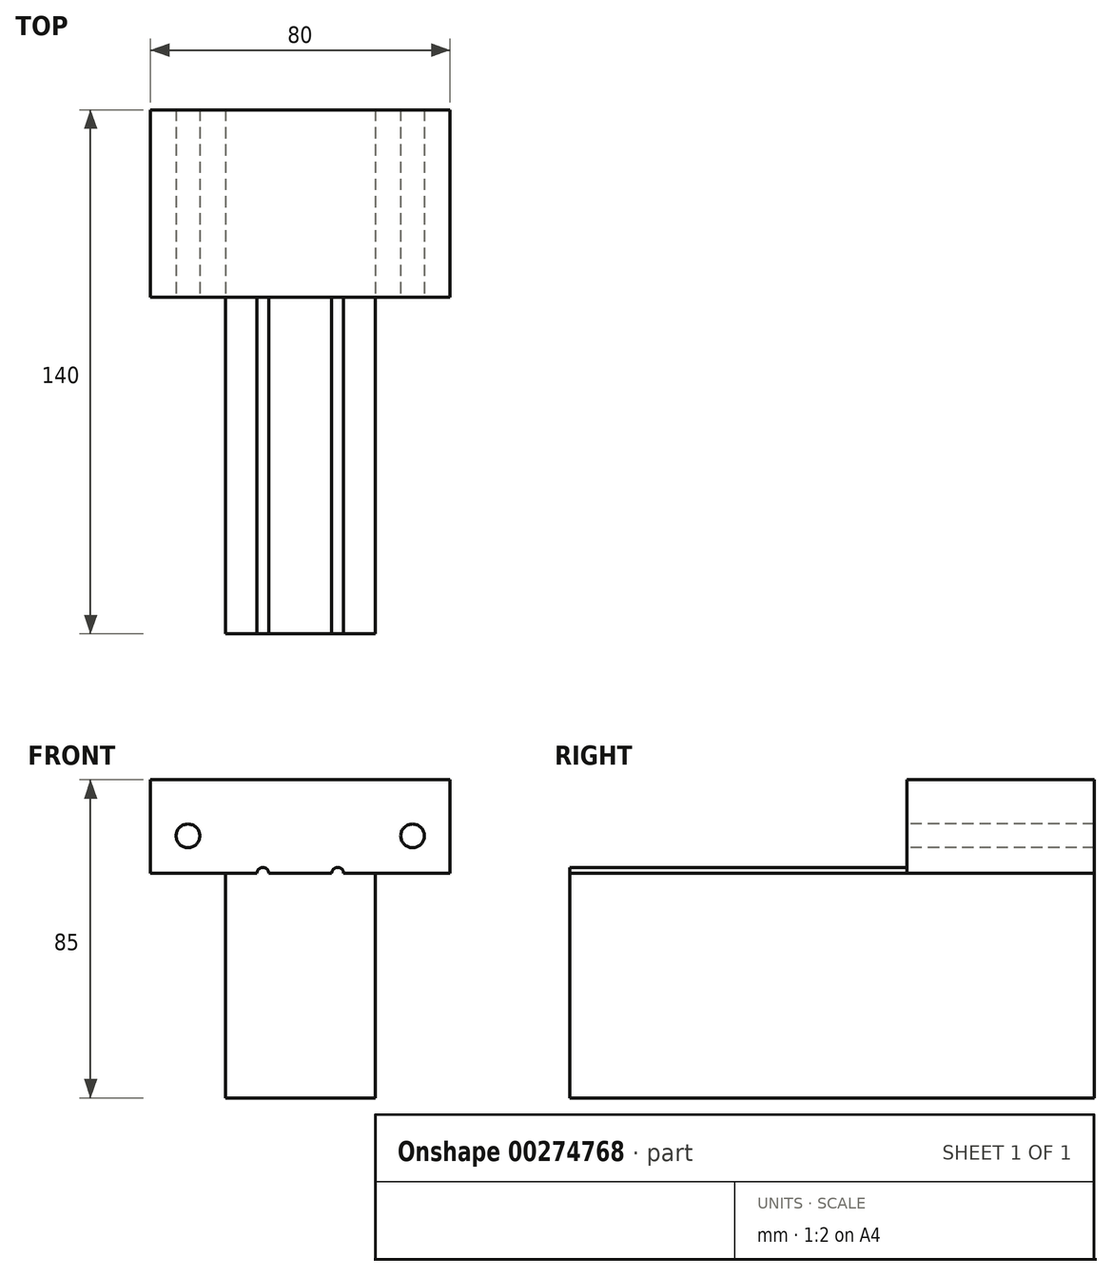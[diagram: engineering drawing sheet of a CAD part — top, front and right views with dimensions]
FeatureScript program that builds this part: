
annotation { "Feature Type Name" : "Feature", "Feature Type Description" : "" }
export const myFeature = defineFeature(function(context is Context, id is Id, definition is map)
    precondition{}
    {
        {
            var Q0;
            Q0=qCreatedBy(makeId("Front.planeOp"),FACE);
            var sketch = newSketch(context, id + "F0", { "sketchPlane" : qUnion([Q0])});
            skLineSegment(sketch, "E0.bottom", {"start": v(20, 30) * mm, "end": v(11.58, 30) * mm});
            skLineSegment(sketch, "E0.top", {"start": v(20, -30) * mm, "end": v(-20, -30) * mm});
            skLineSegment(sketch, "E0.left", {"start": v(20, 30) * mm, "end": v(20, -30) * mm});
            skLineSegment(sketch, "E0.right", {"start": v(-20, 30) * mm, "end": v(-20, -30) * mm});
            skPoint(sketch, "E0.middle", {"position": v(0, 0) * mm});
            skArc(sketch, "E1", {"start": v(-8.4, 30) * mm, "mid": v(-10, 31.59) * mm, "end": v(-11.58, 30) * mm});
            skArc(sketch, "E2", {"start": v(11.58, 30) * mm, "mid": v(10, 31.59) * mm, "end": v(8.4, 30) * mm});
            skLineSegment(sketch, "E3.bottom", {"start": v(-20, 30) * mm, "end": v(-11.58, 30) * mm});
            skLineSegment(sketch, "E3.top", {"start": v(-20, 55) * mm, "end": v(20, 55) * mm});
            skLineSegment(sketch, "E3.left", {"start": v(-20, 30) * mm, "end": v(-20, 55) * mm});
            skLineSegment(sketch, "E3.right", {"start": v(20, 30) * mm, "end": v(20, 55) * mm});
            skLineSegment(sketch, "E4.trimOffspring", {"start": v(-8.4, 30) * mm, "end": v(8.4, 30) * mm});
            skLineSegment(sketch, "E5.trimOffspring", {"start": v(-11.58, 30) * mm, "end": v(-20, 30) * mm});
            skLineSegment(sketch, "E6.trimOffspring", {"start": v(11.58, 30) * mm, "end": v(20, 30) * mm});
            skLineSegment(sketch, "E7.trimOffspring", {"start": v(8.4, 30) * mm, "end": v(-8.4, 30) * mm});
            skLineSegment(sketch, "E8.bottom", {"start": v(20, 55) * mm, "end": v(40, 55) * mm});
            skLineSegment(sketch, "E8.top", {"start": v(20, 30) * mm, "end": v(40, 30) * mm});
            skLineSegment(sketch, "E8.left", {"start": v(20, 55) * mm, "end": v(20, 30) * mm});
            skLineSegment(sketch, "E8.right", {"start": v(40, 55) * mm, "end": v(40, 30) * mm});
            skLineSegment(sketch, "E9", {"start": v(0, 55) * mm, "end": v(0, 30) * mm});
            skPoint(sketch, "E10.MirrorCS.start.orphan", {"position": v(-20, 55) * mm});
            skPoint(sketch, "E11.MirrorCS.start.orphan", {"position": v(-20, 30) * mm});
            skLineSegment(sketch, "E12.MirrorCS", {"start": v(-20, 55) * mm, "end": v(-20, 30) * mm});
            skPoint(sketch, "E13.orphan", {"position": v(-20, 42.5) * mm});
            skPoint(sketch, "E14.start.orphan", {"position": v(30, 55) * mm});
            skPoint(sketch, "E15.start.orphan", {"position": v(20, 42.5) * mm});
            skPoint(sketch, "E16.trimOffspring.end.orphan", {"position": v(40, 42.5) * mm});
            skPoint(sketch, "E17.trimOffspring.end.orphan", {"position": v(30, 30) * mm});
            skLineSegment(sketch, "E18", {"start": v(30, 55) * mm, "end": v(30, 30) * mm});
            skLineSegment(sketch, "E19", {"start": v(20, 40) * mm, "end": v(40, 40) * mm});
            skCircle(sketch, "E20", {"center": v(30, 40) * mm, "radius": 3.18 * mm});
            skLineSegment(sketch, "E21.MirrorCS", {"start": v(-40, 55) * mm, "end": v(-40, 30) * mm});
            skPoint(sketch, "E22.MirrorP", {"position": v(-40, 42.5) * mm});
            skLineSegment(sketch, "E23.MirrorCS", {"start": v(-20, 55) * mm, "end": v(-40, 55) * mm});
            skCircle(sketch, "E24.MirrorC", {"center": v(-30, 40) * mm, "radius": 3.18 * mm});
            skPoint(sketch, "E25.MirrorP", {"position": v(-30, 55) * mm});
            skLineSegment(sketch, "E26.MirrorCS", {"start": v(-20, 30) * mm, "end": v(-40, 30) * mm});
            skLineSegment(sketch, "E27.MirrorCS", {"start": v(-20, 40) * mm, "end": v(-40, 40) * mm});
            skLineSegment(sketch, "E28.MirrorCS", {"start": v(-30, 55) * mm, "end": v(-30, 30) * mm});
            skPoint(sketch, "E29.MirrorP", {"position": v(-30, 30) * mm});
            skSolve(sketch);
        }
        {
            var Q0;
            Q0=makeQuery(id+"F0.imprint","IMPRINT",FACE,{"disambiguationData":[TD([[makeQuery(id+"F0.imprint","IMPRINT",EDGE,{"derivedFrom":sQuery(id+"F0.wireOp",EDGE,"E0.top")}),-1.0]])]});
            extrude(context, id + "F1", {"entities" : qUnion([Q0]), "depth" : 90 * mm});
        }
        {
            var Q0;
            Q0 = qSketchRegion(id + "F0", true);
            extrude(context, id + "F2", {"entities" : qUnion([Q0]), "operationType" : NewBodyOperationType.ADD, "oppositeDirection" : true, "depth" : 50 * mm});
        }
    });
